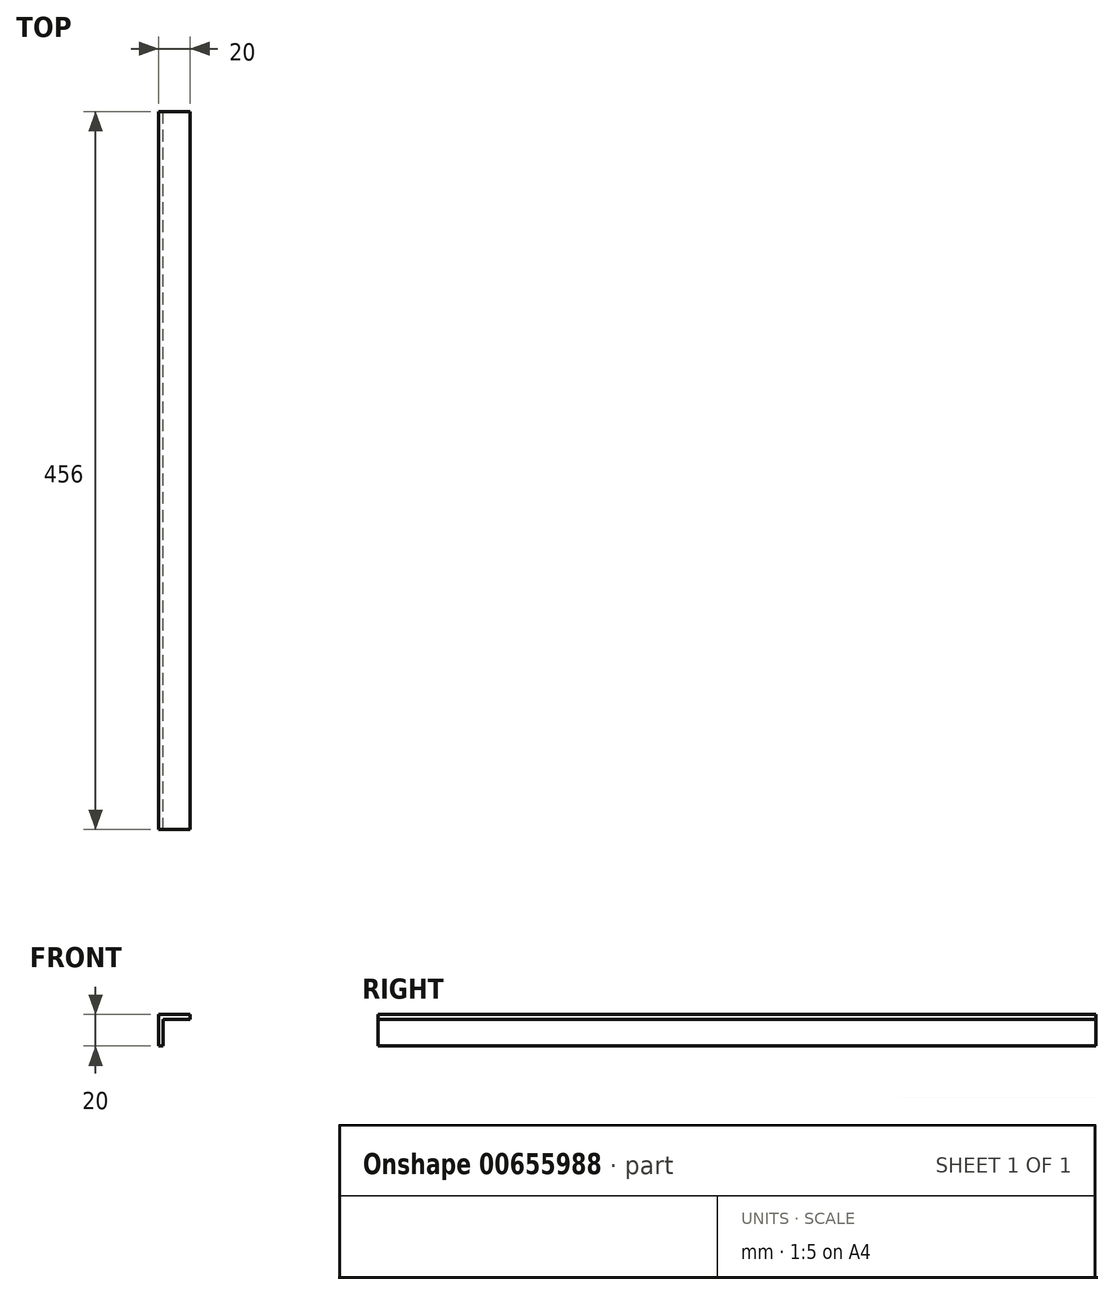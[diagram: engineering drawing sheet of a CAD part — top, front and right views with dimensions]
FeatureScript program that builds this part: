
annotation { "Feature Type Name" : "Feature", "Feature Type Description" : "" }
export const myFeature = defineFeature(function(context is Context, id is Id, definition is map)
    precondition{}
    {
        {
            var Q0;
            Q0=qCreatedBy(makeId("Front.planeOp"),FACE);
            var sketch = newSketch(context, id + "F0", { "sketchPlane" : qUnion([Q0])});
            skLineSegment(sketch, "E0", {"start": v(0, 0) * mm, "end": v(0, 20) * mm});
            skLineSegment(sketch, "E1", {"start": v(0, 20) * mm, "end": v(20, 20) * mm});
            skLineSegment(sketch, "E2.0", {"start": v(3, 17) * mm, "end": v(20, 17) * mm});
            skLineSegment(sketch, "E2.1", {"start": v(3, 0) * mm, "end": v(3, 17) * mm});
            skLineSegment(sketch, "E3", {"start": v(20, 20) * mm, "end": v(20, 17) * mm});
            skLineSegment(sketch, "E4", {"start": v(0, 0) * mm, "end": v(3, 0) * mm});
            skSolve(sketch);
        }
        {
            var Q0;
            Q0=makeQuery(id+"F0.imprint","IMPRINT",FACE,{"disambiguationData":[TD([[makeQuery(id+"F0.imprint","IMPRINT",EDGE,{"derivedFrom":sQuery(id+"F0.wireOp",EDGE,"E0")}),-1.0]])]});
            extrude(context, id + "F1", {"entities" : qUnion([Q0]), "depth" : 496 * mm - 40 * mm, "offsetDistance" : 25.4 * mm});
        }
    });
